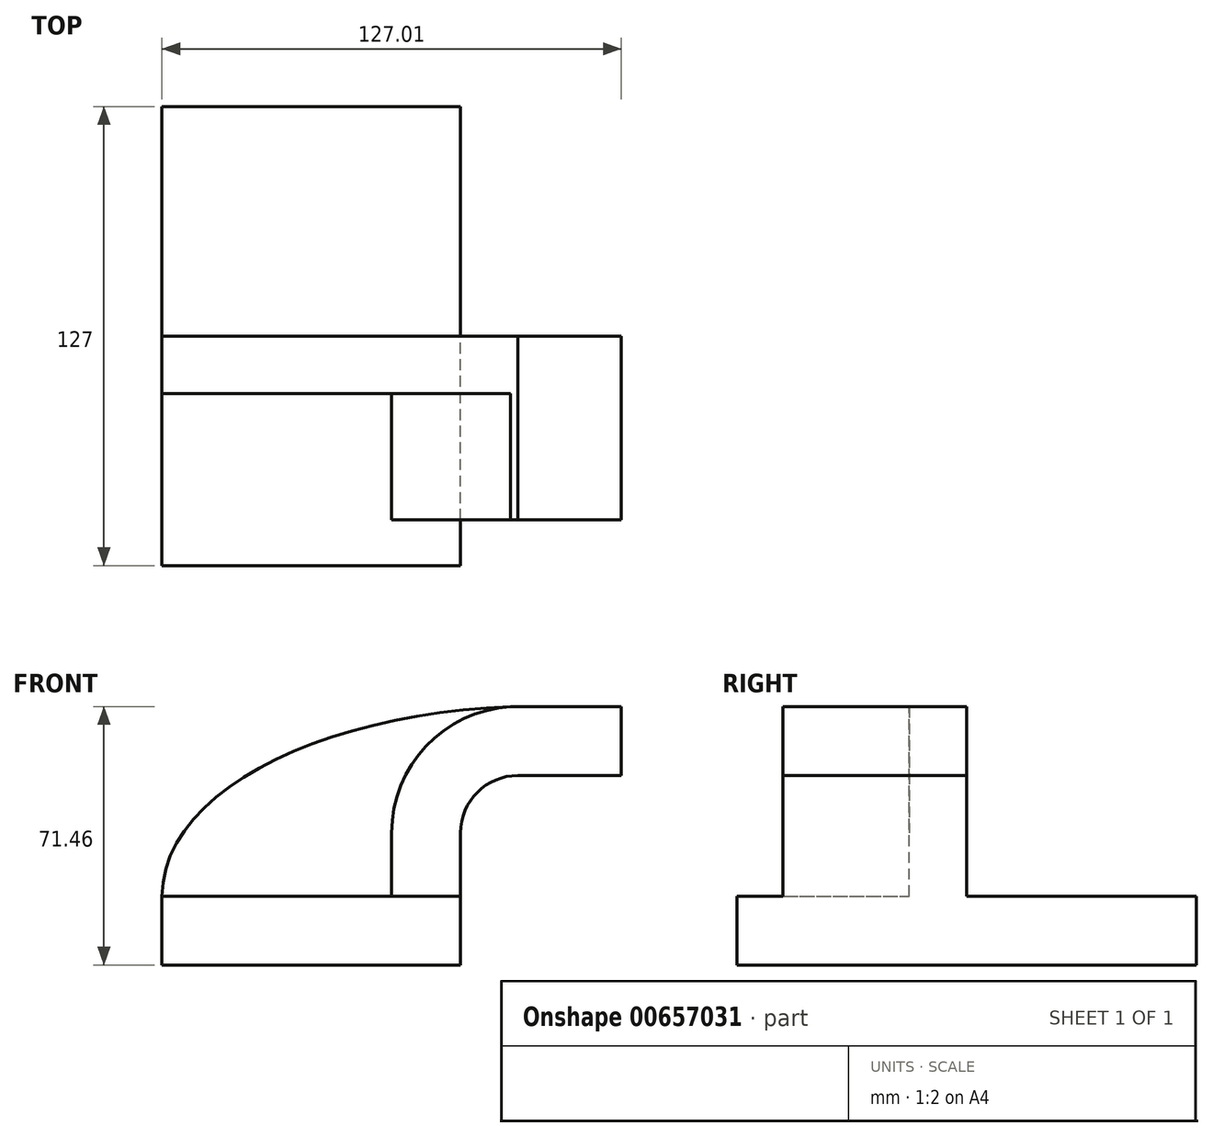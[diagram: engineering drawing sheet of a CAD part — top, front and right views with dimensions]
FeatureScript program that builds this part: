
annotation { "Feature Type Name" : "Feature", "Feature Type Description" : "" }
export const myFeature = defineFeature(function(context is Context, id is Id, definition is map)
    precondition{}
    {
        {
            var Q0;
            Q0=qCreatedBy(makeId("Front.planeOp"),FACE);
            var sketch = newSketch(context, id + "F0", { "sketchPlane" : qUnion([Q0])});
            skLineSegment(sketch, "E0.bottom", {"start": v(-41.28, 9.52) * mm, "end": v(41.27, 9.53) * mm});
            skLineSegment(sketch, "E0.top", {"start": v(-41.28, -9.53) * mm, "end": v(41.28, -9.53) * mm});
            skLineSegment(sketch, "E0.left", {"start": v(-41.28, 9.52) * mm, "end": v(-41.28, -9.53) * mm});
            skLineSegment(sketch, "E0.right", {"start": v(41.27, 9.53) * mm, "end": v(41.28, -9.52) * mm});
            skPoint(sketch, "E0.middle", {"position": v(0, 0) * mm});
            skLineSegment(sketch, "E1.bottom", {"start": v(60.32, 38.1) * mm, "end": v(111.12, 38.1) * mm});
            skLineSegment(sketch, "E1.top", {"start": v(60.32, 66.67) * mm, "end": v(111.12, 66.67) * mm});
            skLineSegment(sketch, "E1.left", {"start": v(60.32, 38.1) * mm, "end": v(60.32, 66.67) * mm});
            skLineSegment(sketch, "E1.right", {"start": v(111.12, 38.1) * mm, "end": v(111.12, 66.67) * mm});
            skPoint(sketch, "E1.middle", {"position": v(85.72, 52.39) * mm});
            skLineSegment(sketch, "E2", {"start": v(41.27, 9.53) * mm, "end": v(41.27, 27) * mm});
            skArc(sketch, "E3", {"start": v(41.27, 27) * mm, "mid": v(45.92, 38.23) * mm, "end": v(57.15, 42.88) * mm});
            skLineSegment(sketch, "E4", {"start": v(57.15, 42.88) * mm, "end": v(85.81, 42.88) * mm});
            skLineSegment(sketch, "E5.0", {"start": v(57.15, 61.93) * mm, "end": v(85.72, 61.93) * mm});
            skArc(sketch, "E5.1", {"start": v(22.22, 27) * mm, "mid": v(32.45, 51.7) * mm, "end": v(57.15, 61.93) * mm});
            skLineSegment(sketch, "E5.2", {"start": v(22.22, 9.53) * mm, "end": v(22.22, 27) * mm});
            skLineSegment(sketch, "E6", {"start": v(85.72, 38.1) * mm, "end": v(85.72, 66.67) * mm});
            skFitSpline(sketch, "E7", {"points": [v(-41.28, 9.52) * mm, v(57.15, 61.93) * mm], "startDerivative": vector(0.89, 90.08) * mm, "endDerivative": vector(155.6, 3.72) * mm});
            skSolve(sketch);
        }
        {
            var Q0;
            Q0=makeQuery(id+"F0.imprint","IMPRINT",FACE,{"disambiguationData":[TD([[makeQuery(id+"F0.imprint","IMPRINT",EDGE,{"derivedFrom":sQuery(id+"F0.wireOp",EDGE,"E0.top")}),1.0]])]});
            extrude(context, id + "F1", {"entities" : qUnion([Q0]), "endBound" : BoundingType.SYMMETRIC, "depth" : 127 * mm, "offsetDistance" : 25.4 * mm});
        }
        {
            var Q0;
            {var subQ1=sQuery(id+"F0.wireOp",EDGE,"E2");Q0=makeQuery(id+"F0.imprint","IMPRINT",FACE,{"disambiguationData":[TD([[makeQuery(id+"F0.imprint","IMPRINT",EDGE,{"derivedFrom":subQ1}),1.0]])]});}
            var Q1;
            {var subQ0=sQuery(id+"F0.wireOp",EDGE,"E4");var subQ1=sQuery(id+"F0.wireOp",EDGE,"E1.left");var subQ2=makeQuery(id+"F0.imprint","INTERSECT",VERTEX,{"derivedFrom":[subQ1,subQ0]});Q1=makeQuery(id+"F0.imprint","IMPRINT",FACE,{"disambiguationData":[TD([[makeQuery(id+"F0.imprint","IMPRINT",EDGE,{"disambiguationData":[TD([[subQ2,-1.0]])],"derivedFrom":subQ1}),-1.0]])]});}
            extrude(context, id + "F2", {"entities" : qUnion([Q0, Q1]), "operationType" : NewBodyOperationType.ADD, "depth" : 50.8 * mm, "offsetDistance" : 25.4 * mm});
        }
        {
            var Q0;
            {var subQ3=sQuery(id+"F0.wireOp",EDGE,"E5.2");Q0=makeQuery(id+"F0.imprint","IMPRINT",FACE,{"disambiguationData":[TD([[makeQuery(id+"F0.imprint","IMPRINT",EDGE,{"derivedFrom":subQ3}),1.0]])]});}
            extrude(context, id + "F3", {"entities" : qUnion([Q0]), "operationType" : NewBodyOperationType.ADD, "depth" : 15.88 * mm, "offsetDistance" : 25.4 * mm});
        }
    });
